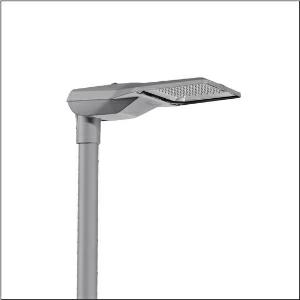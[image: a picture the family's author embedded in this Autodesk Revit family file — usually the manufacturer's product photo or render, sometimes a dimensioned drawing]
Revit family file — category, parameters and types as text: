
# Revit family: streetlight_sl_21_iq_midi___st1_0a_5xe3d31v08mb_ff90
name_source: partatom
category: Lighting Fixtures
units: mm (PartAtom-declared; Revit-internal decimal feet)

## family parameters
Cut with Voids When Loaded = No
Host = Face
Light Source = No
Part Type = Normal
Room Calculation Point = No
Round Connector Dimension = Use Diameter
Shared = No

## types (1)
- --- (1 x LED, 18340 lm, 129.3 W, 3000K)
    Apparent Load = 129 VA
    CIE Flux Codes = 37 72 97 100 100
    Color Rendering = 70
    Color Temperature = 3000K
    Default Elevation = 1800 mm
    Description = Streetlight SL 21 iQ midi, mast luminaire, primary light control with lens, of PMMA, primary optical cover: cover, of toughened safety glass, transparent, light distribution: ST1.0a, light emission: direct distribution, primary light characteristic: asymmetric, installation type: post-top, side-entry, LED, High Power LED, rated luminous flux: 18.340lm, luminous efficacy: 142lm/W, light colour: 730, colour temperature: 3000K, control: presetting dimming logarithmic, Street-Remote, Auto-Match, Temp-Guard, Lumen-Switch, Night-Set, Smart-Wire, Light-Fading, Desk-Remote (wireless, voltage-free reading and setting of iQ features in the workshop via application-optimized NFC function/RFID function), optimised constant luminous flux control (CLO 2.0), mains connection: 230..240V, AC, 50/60Hz, start of lifetime: 129W, end of service life: 142W, reduction: 56W, luminaire housing, of diecast aluminium, powder-coated, Siteco® metallic grey (DB 702S), corrosivity category C5 mid according to DIN EN ISO 12944, please order mast flange separately, inclination adjustable: 0°, 5°, 10°, 15°, sealing non-destructively replaceable, multi-level sealing system, length: 644mm, width: 335mm, height: 110mm, mast flange for spigot size: 42mm (side-entry): 5XC10008XM4, 60/48mm (side-entry/post-top): 5XC10108XM2, 76/60mm (side-entry/post-top): 5XC10108XM1, Smart Interface above, protection rating (complete): IP66, insulation class (complete): insulation class II (safety insulation), certification: CE, ENEC, ENEC+, VDE, impact resistance: IK09, permissible operating ambient temperature for outdoor applications: -40..+50°C, standard-compliant lighting for roads and squares, packaging unit: 1 piece

Light Distribution: ST1.0a
    Height = 111 mm
    Lamp = 1 x LED
    Lamp Light Flux = 18340 lm
    Lamp Power = 129.3 W
    Lamp count = 1
    Length = 644 mm
    Luminous efficacy = 142 lm/W
    Manufacturer = Siteco
    ModVariant = No
    Model = 5XE3D31V08MB
    Number of Poles = 1
    OnlyDefault = Yes
    Power Factor = 1
    Product Name = Streetlight SL 21 iQ midi | ST1.0a
    Product group = mast luminaire | pylon top
    ProductGroupID = 6100
    Protection Class = Protection class II
    Protection Degree = IP 66
    RLX_Detail_Level = 1
    RLX_Emergency_Light_Flux = 0 lm
    RLX_Emergency_Type = 0
    RLX_Emergency_Type_DB = No
    RlxData = <blob elided: 90809 chars, md5=e21ec9f3>
    Socket = socket
    Standby Power = 0 W
    System Light Flux = 18340 lm
    System Power = 129 W
    Type Comments = factory setting: luminous flux: 100 % | dim-lin: 254 | 672 mA
    Type Image = l_1004302.jpg
    URL = http://relux.com
    VarID = @adj_044683
    Voltage = 0 V
    Weight = 0.00 kg
    Width = 336 mm

## geometry (parser evidence)
native form markers: Blend x4, Sweep x11
no freeform markers — native parametric forms only
